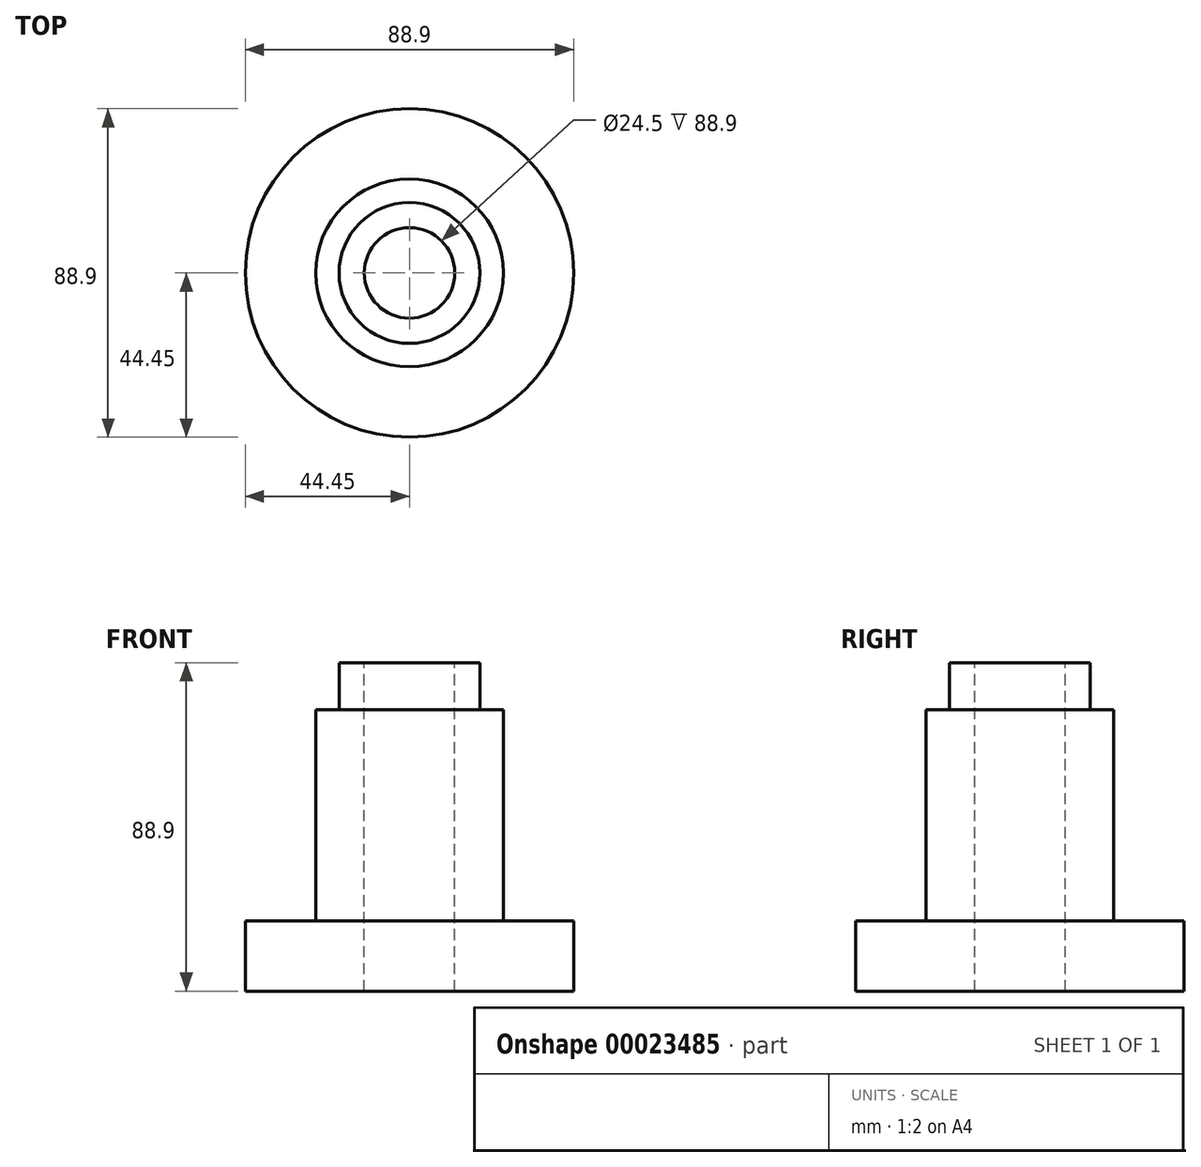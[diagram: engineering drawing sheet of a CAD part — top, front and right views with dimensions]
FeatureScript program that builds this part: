
annotation { "Feature Type Name" : "Feature", "Feature Type Description" : "" }
export const myFeature = defineFeature(function(context is Context, id is Id, definition is map)
    precondition{}
    {
        {
            var Q0;
            Q0=qCreatedBy(makeId("Front.planeOp"),FACE);
            var sketch = newSketch(context, id + "F0", { "sketchPlane" : qUnion([Q0])});
            skLineSegment(sketch, "E0", {"start": v(0, 145.72) * mm, "end": v(0, -77.52) * mm, "construction": true});
            skLineSegment(sketch, "E1.bottom", {"start": v(12.25, -77.52) * mm, "end": v(44.45, -77.52) * mm});
            skLineSegment(sketch, "E1.top", {"start": v(12.25, -58.47) * mm, "end": v(44.45, -58.47) * mm});
            skLineSegment(sketch, "E1.left", {"start": v(12.25, -77.52) * mm, "end": v(12.25, -58.47) * mm});
            skLineSegment(sketch, "E1.right", {"start": v(44.45, -77.52) * mm, "end": v(44.45, -58.47) * mm});
            skLineSegment(sketch, "E2.bottom", {"start": v(12.25, -58.47) * mm, "end": v(25.4, -58.47) * mm});
            skLineSegment(sketch, "E2.top", {"start": v(12.25, -1.32) * mm, "end": v(25.4, -1.32) * mm});
            skLineSegment(sketch, "E2.left", {"start": v(12.25, -58.47) * mm, "end": v(12.25, -1.32) * mm});
            skLineSegment(sketch, "E2.right", {"start": v(25.4, -58.47) * mm, "end": v(25.4, -1.32) * mm});
            skLineSegment(sketch, "E3.bottom", {"start": v(12.25, -1.32) * mm, "end": v(19.05, -1.32) * mm});
            skLineSegment(sketch, "E3.top", {"start": v(12.25, 11.38) * mm, "end": v(19.05, 11.38) * mm});
            skLineSegment(sketch, "E3.left", {"start": v(12.25, -1.32) * mm, "end": v(12.25, 11.38) * mm});
            skLineSegment(sketch, "E3.right", {"start": v(19.05, -1.32) * mm, "end": v(19.05, 11.38) * mm});
            skSolve(sketch);
        }
        {
            var Q0;
            Q0 = qSketchRegion(id + "F0", true);
            var Q1;
            Q1=sQuery(id+"F0.wireOp",EDGE,"E0");
            revolve(context, id + "F1", {"entities" : qUnion([Q0]), "axis" : qUnion([Q1]), "revolveType" : RevolveType.FULL});
        }
    });
